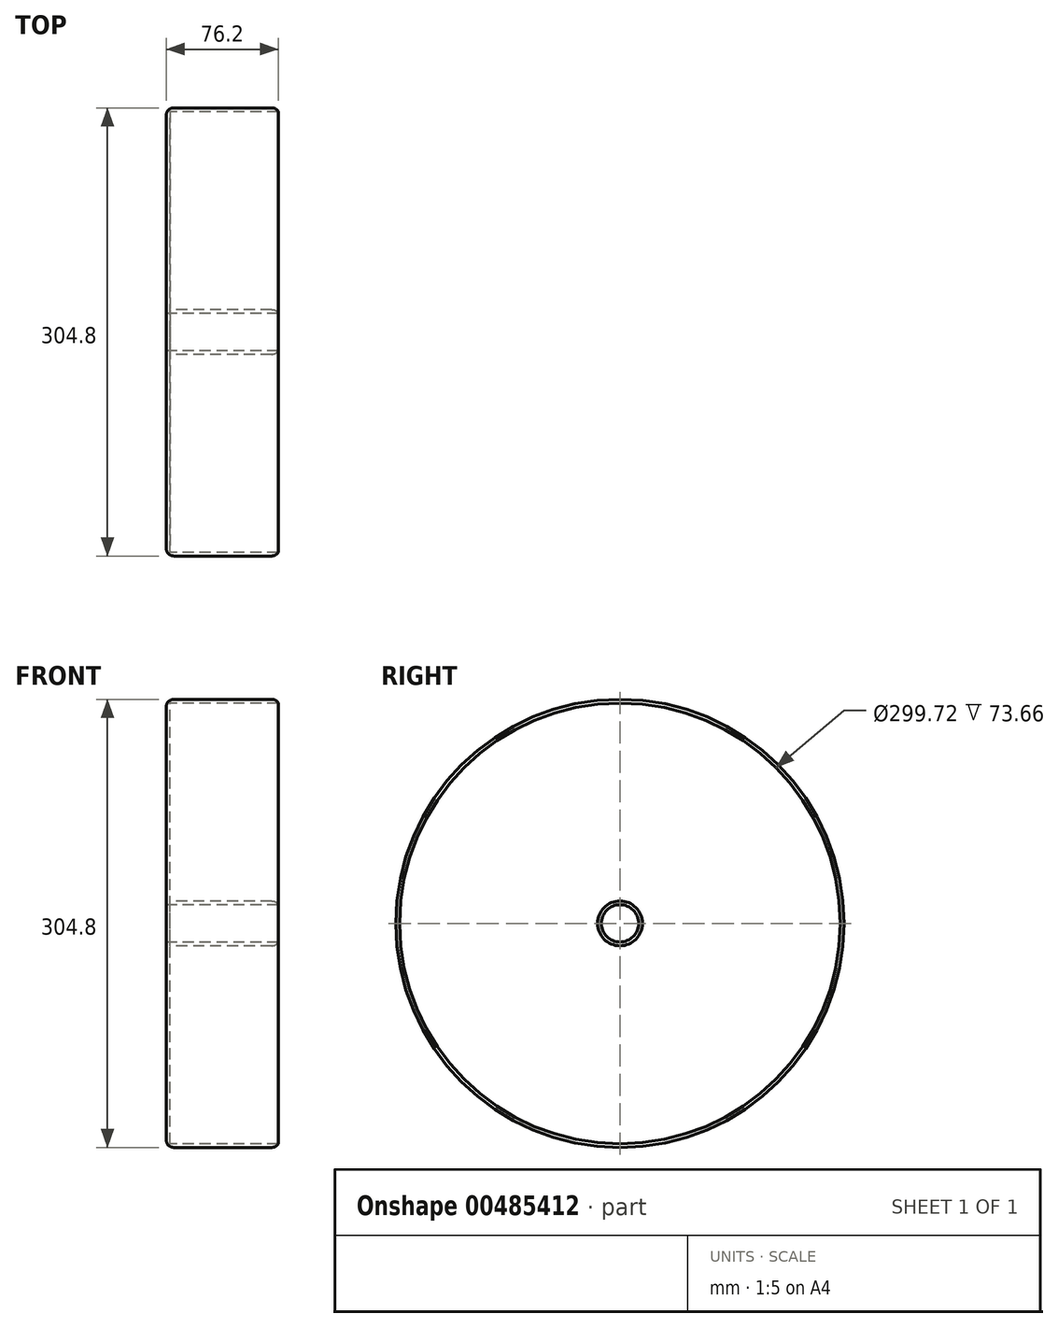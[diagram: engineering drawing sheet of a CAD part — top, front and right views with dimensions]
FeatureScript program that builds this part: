
annotation { "Feature Type Name" : "Feature", "Feature Type Description" : "" }
export const myFeature = defineFeature(function(context is Context, id is Id, definition is map)
    precondition{}
    {
        {
            var Q0;
            Q0=qCreatedBy(makeId("Right.planeOp"),FACE);
            var sketch = newSketch(context, id + "F0", { "sketchPlane" : qUnion([Q0])});
            skCircle(sketch, "E0", {"center": v(0, 0) * mm, "radius": 152.4 * mm});
            skCircle(sketch, "E1", {"center": v(0, 0) * mm, "radius": 12.7 * mm});
            skSolve(sketch);
        }
        {
            var Q0;
            Q0=makeQuery(id+"F0.imprint","IMPRINT",FACE,{"disambiguationData":[TD([[makeQuery(id+"F0.imprint","IMPRINT",EDGE,{"derivedFrom":sQuery(id+"F0.wireOp",EDGE,"E0")}),1.0]])]});
            extrude(context, id + "F1", {"entities" : qUnion([Q0]), "depth" : 76.2 * mm});
        }
        {
            var Q0;
            Q0=makeQuery(id+"F1.opExtrude","CAP_FACE",FACE,{"disambiguationData":[OSD([sQuery(id+"F0.wireOp",EDGE,"E0")])],"isStart":false});
            shell(context, id + "F2", {"entities" : qUnion([Q0]), "thickness" : 2.54 * mm});
        }
        {
            var Q0;
            Q0=makeQuery(id+"F1.opExtrude","CAP_EDGE",EDGE,{"disambiguationData":[OSD([sQuery(id+"F0.wireOp",EDGE,"E0")])],"isStart":false});
            var Q1;
            {var subQ0=sQuery(id+"F0.wireOp",EDGE,"E1");Q1=makeQuery(id+"F2.opShell","OFFSET_EDGE",EDGE,{"disambiguationData":[OSD([subQ0]),TDD([makeQuery(id+"F1.opExtrude","CAP_EDGE",EDGE,{"disambiguationData":[OSD([subQ0])],"isStart":false})])]});}
            fillet(context, id + "F3", {"entities" : qUnion([Q0, Q1]), "radius" : 5.08 * mm, "tangentPropagation" : true, "allowEdgeOverflow" : false});
        }
        {
            var Q0;
            Q0=makeQuery(id+"F1.opExtrude","SWEPT_FACE",FACE,{"disambiguationData":[OSD([sQuery(id+"F0.wireOp",EDGE,"E0")])]});
            fillet(context, id + "F4", {"entities" : qUnion([Q0]), "radius" : 5.08 * mm, "tangentPropagation" : true, "allowEdgeOverflow" : false});
        }
    });
